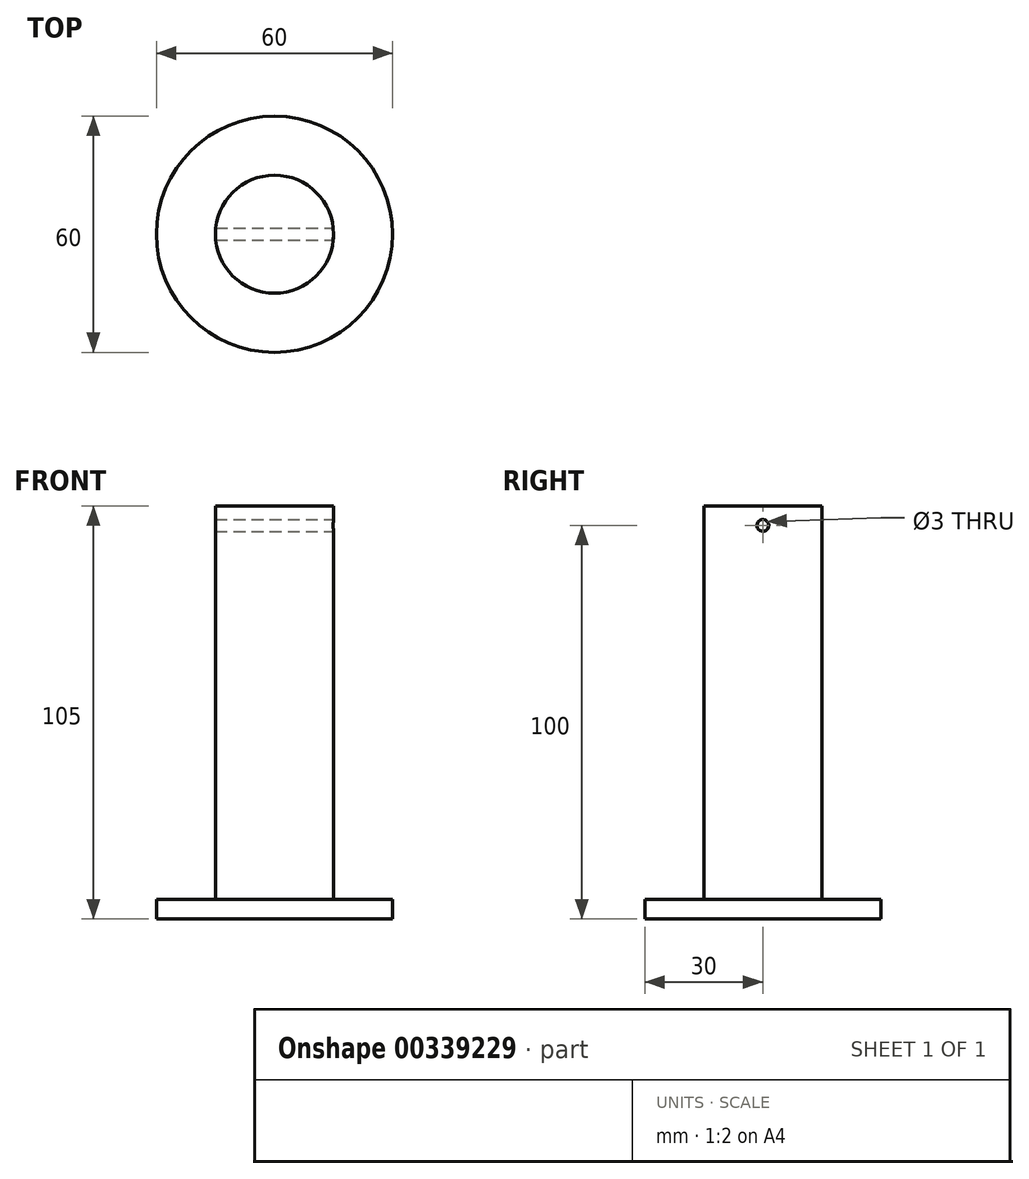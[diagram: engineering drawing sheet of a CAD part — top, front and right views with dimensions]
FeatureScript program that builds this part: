
annotation { "Feature Type Name" : "Feature", "Feature Type Description" : "" }
export const myFeature = defineFeature(function(context is Context, id is Id, definition is map)
    precondition{}
    {
        {
            var Q0;
            Q0=qCreatedBy(makeId("Front.planeOp"),FACE);
            var sketch = newSketch(context, id + "F0", { "sketchPlane" : qUnion([Q0])});
            skLineSegment(sketch, "E0.bottom", {"start": v(0, 0) * mm, "end": v(15, 0) * mm});
            skLineSegment(sketch, "E0.top", {"start": v(0, 100) * mm, "end": v(15, 100) * mm});
            skLineSegment(sketch, "E0.left", {"start": v(0, 0) * mm, "end": v(0, 100) * mm});
            skLineSegment(sketch, "E0.right", {"start": v(15, 0) * mm, "end": v(15, 100) * mm});
            skLineSegment(sketch, "E1.bottom", {"start": v(0, 0) * mm, "end": v(30, 0) * mm});
            skLineSegment(sketch, "E1.top", {"start": v(0, -5) * mm, "end": v(30, -5) * mm});
            skLineSegment(sketch, "E1.left", {"start": v(0, 0) * mm, "end": v(0, -5) * mm});
            skLineSegment(sketch, "E1.right", {"start": v(30, 0) * mm, "end": v(30, -5) * mm});
            skSolve(sketch);
        }
        {
            var Q0;
            Q0=makeQuery(id+"F0.imprint","IMPRINT",FACE,{"disambiguationData":[TD([[makeQuery(id+"F0.imprint","IMPRINT",EDGE,{"derivedFrom":sQuery(id+"F0.wireOp",EDGE,"E0.top")}),-1.0]])]});
            var Q1;
            Q1=makeQuery(id+"F0.imprint","IMPRINT",FACE,{"disambiguationData":[TD([[makeQuery(id+"F0.imprint","IMPRINT",EDGE,{"derivedFrom":sQuery(id+"F0.wireOp",EDGE,"E1.top")}),1.0]])]});
            var Q2;
            Q2=sQuery(id+"F0.wireOp",EDGE,"E0.left");
            revolve(context, id + "F1", {"entities" : qUnion([Q0, Q1]), "axis" : qUnion([Q2]), "revolveType" : RevolveType.FULL});
        }
        {
            var Q0;
            Q0=qCreatedBy(makeId("Right.planeOp"),FACE);
            var sketch = newSketch(context, id + "F2", { "sketchPlane" : qUnion([Q0])});
            skCircle(sketch, "E2", {"center": v(0, 95) * mm, "radius": 1.5 * mm});
            skLineSegment(sketch, "E3", {"start": v(0, 0) * mm, "end": v(0, 110.49) * mm, "construction": true});
            skSolve(sketch);
        }
        {
            var Q0;
            Q0 = qSketchRegion(id + "F2", true);
            extrude(context, id + "F3", {"entities" : qUnion([Q0]), "operationType" : NewBodyOperationType.REMOVE, "oppositeDirection" : true, "depth" : 25 * mm, "hasSecondDirection" : true, "secondDirectionOppositeDirection" : false, "secondDirectionDepth" : 25 * mm});
        }
    });
